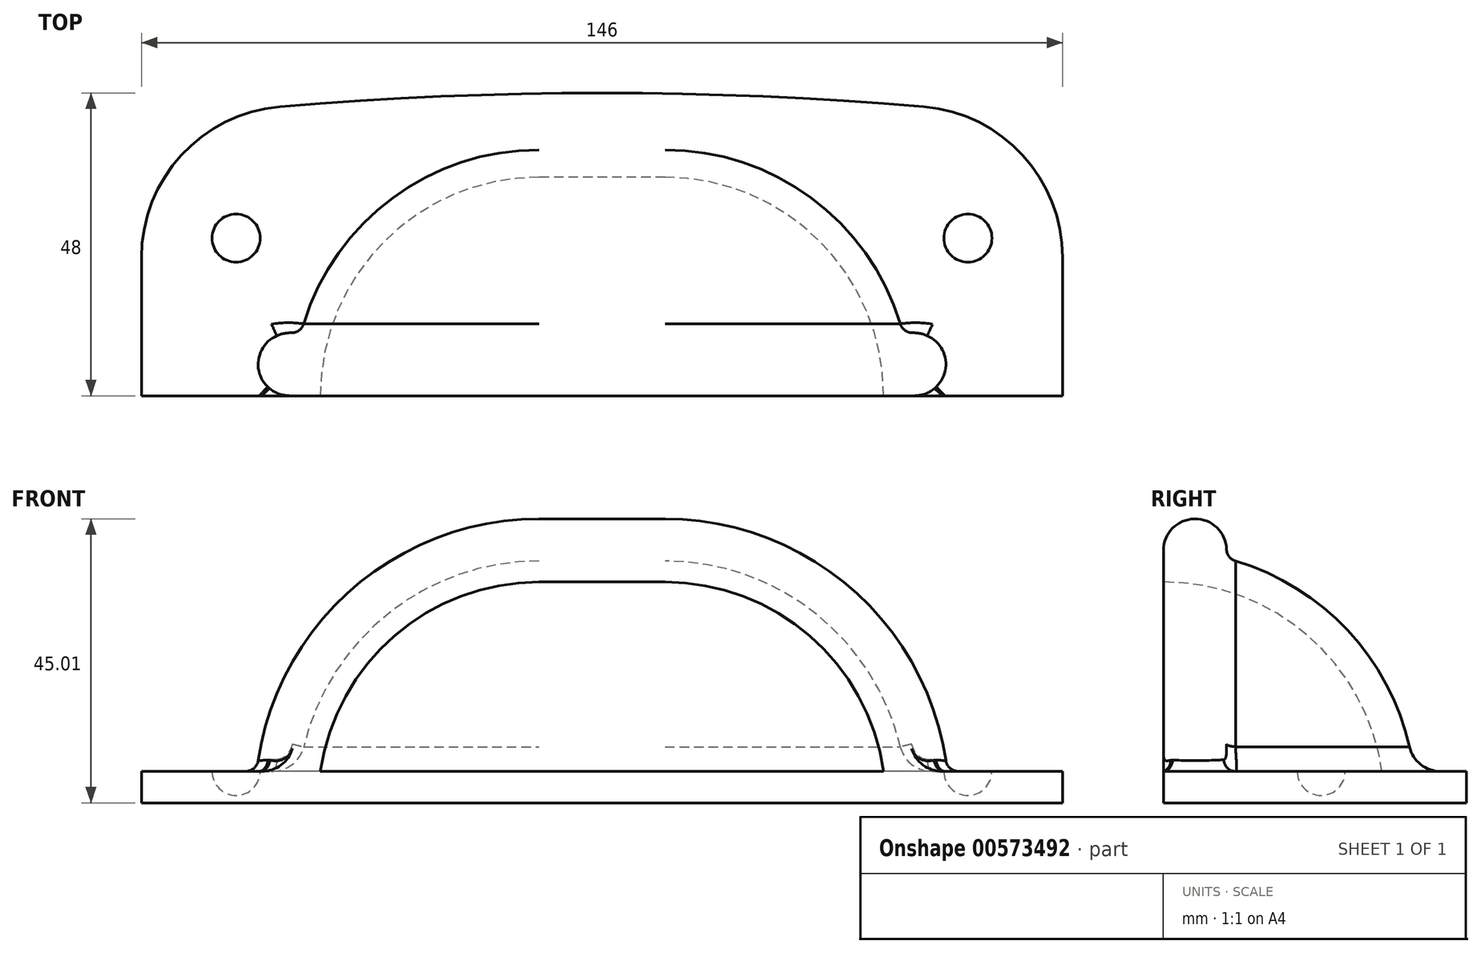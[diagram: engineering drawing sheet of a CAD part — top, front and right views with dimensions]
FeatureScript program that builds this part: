
annotation { "Feature Type Name" : "Feature", "Feature Type Description" : "" }
export const myFeature = defineFeature(function(context is Context, id is Id, definition is map)
    precondition{}
    {
        {
            var Q0;
            Q0=qCreatedBy(makeId("Top.planeOp"),FACE);
            var sketch = newSketch(context, id + "F0", { "sketchPlane" : qUnion([Q0])});
            skLineSegment(sketch, "E0", {"start": v(0, 0) * mm, "end": v(10, 0) * mm, "construction": true});
            skArc(sketch, "E1", {"start": v(10, 35) * mm, "mid": v(34.75, 24.75) * mm, "end": v(45, 0) * mm});
            skLineSegment(sketch, "E2", {"start": v(10, 35) * mm, "end": v(0, 35) * mm});
            skLineSegment(sketch, "E3", {"start": v(45, 0) * mm, "end": v(50, 0) * mm});
            skLineSegment(sketch, "E4.0", {"start": v(10, 40) * mm, "end": v(0, 40) * mm});
            skArc(sketch, "E4.1", {"start": v(10, 40) * mm, "mid": v(38.28, 28.28) * mm, "end": v(50, 0) * mm});
            skLineSegment(sketch, "E5", {"start": v(0, 40) * mm, "end": v(0, 0) * mm, "construction": true});
            skLineSegment(sketch, "E6.MirrorCS", {"start": v(-10, 35) * mm, "end": v(0, 35) * mm});
            skArc(sketch, "E7.MirrorCS", {"start": v(-10, 35) * mm, "mid": v(-34.75, 24.75) * mm, "end": v(-45, 0) * mm});
            skLineSegment(sketch, "E8.MirrorCS", {"start": v(-45, 0) * mm, "end": v(-50, 0) * mm});
            skArc(sketch, "E9.MirrorCS", {"start": v(-10, 40) * mm, "mid": v(-38.28, 28.28) * mm, "end": v(-50, 0) * mm});
            skLineSegment(sketch, "E10.MirrorCS", {"start": v(-10, 40) * mm, "end": v(0, 40) * mm});
            skLineSegment(sketch, "E11.MirrorCS", {"start": v(0, 0) * mm, "end": v(-10, 0) * mm});
            skSolve(sketch);
        }
        {
            var Q0;
            Q0=qSketchRegion(id+"F0",true);
            var Q1;
            Q1=sQuery(id+"F0.wireOp",EDGE,"E0");
            revolve(context, id + "F1", {"entities" : qUnion([Q0]), "axis" : qUnion([Q1]), "revolveType" : RevolveType.ONE_DIRECTION, "angle" : 90 * degree});
        }
        {
            var Q0;
            Q0=qCreatedBy(makeId("Top.planeOp"),FACE);
            var sketch = newSketch(context, id + "F2", { "sketchPlane" : qUnion([Q0])});
            skArc(sketch, "E12", {"start": v(51.04, 45.83) * mm, "mid": v(25.54, 47.46) * mm, "end": v(0, 48) * mm});
            skLineSegment(sketch, "E13", {"start": v(0, 0) * mm, "end": v(0, 48) * mm, "construction": true});
            skLineSegment(sketch, "E14", {"start": v(0, 48) * mm, "end": v(-79.99, 48) * mm, "construction": true});
            skLineSegment(sketch, "E15", {"start": v(0, 0) * mm, "end": v(10, 0) * mm});
            skLineSegment(sketch, "E16", {"start": v(73, 0) * mm, "end": v(73, 21.91) * mm});
            skPoint(sketch, "E17.visualSharp", {"position": v(73, 43.54) * mm});
            skArc(sketch, "E17.filletArc", {"start": v(73, 21.91) * mm, "mid": v(66.68, 38.14) * mm, "end": v(51.04, 45.83) * mm});
            skArc(sketch, "E18.MirrorCS", {"start": v(-51.04, 45.83) * mm, "mid": v(-25.54, 47.46) * mm, "end": v(0, 48) * mm});
            skArc(sketch, "E19.MirrorCS", {"start": v(-73, 21.91) * mm, "mid": v(-66.68, 38.14) * mm, "end": v(-51.04, 45.83) * mm});
            skLineSegment(sketch, "E20.MirrorCS", {"start": v(-73, 0) * mm, "end": v(-73, 21.91) * mm});
            skLineSegment(sketch, "E21.MirrorCS", {"start": v(0, 0) * mm, "end": v(-10, 0) * mm});
            skArc(sketch, "E22.0", {"start": v(-10, 35) * mm, "mid": v(-34.75, 24.75) * mm, "end": v(-45, 0) * mm});
            skLineSegment(sketch, "E22.1", {"start": v(10, 35) * mm, "end": v(-10, 35) * mm});
            skArc(sketch, "E22.2", {"start": v(10, 35) * mm, "mid": v(34.75, 24.75) * mm, "end": v(45, 0) * mm});
            skLineSegment(sketch, "E23.trimOffspring", {"start": v(-45, 0) * mm, "end": v(-73, 0) * mm});
            skLineSegment(sketch, "E24.trimOffspring", {"start": v(45, 0) * mm, "end": v(73, 0) * mm});
            skSolve(sketch);
        }
        {
            var Q0;
            Q0=qSketchRegion(id+"F2",true);
            extrude(context, id + "F3", {"entities" : qUnion([Q0]), "operationType" : NewBodyOperationType.ADD, "depth" : 5 * mm});
        }
        {
            var Q0;
            Q0=qCreatedBy(makeId("Right.planeOp"),FACE);
            var sketch = newSketch(context, id + "F4", { "sketchPlane" : qUnion([Q0])});
            skArc(sketch, "E25.0.0", {"start": v(10, 33.54) * mm, "mid": v(5.05, 34.63) * mm, "end": v(0, 35) * mm});
            skArc(sketch, "E25.0.2", {"start": v(0, 35) * mm, "mid": v(5.05, 34.63) * mm, "end": v(10, 33.54) * mm});
            skLineSegment(sketch, "E26", {"start": v(0, 35) * mm, "end": v(0, 40) * mm});
            skArc(sketch, "E27", {"start": v(0, 40) * mm, "mid": v(5, 45) * mm, "end": v(10, 40) * mm});
            skLineSegment(sketch, "E28", {"start": v(10, 40) * mm, "end": v(10, 33.54) * mm});
            skPoint(sketch, "E29.orphan", {"position": v(35, 0) * mm});
            skSolve(sketch);
        }
        {
            var Q0;
            Q0=makeQuery(id+"F3.boolean.opBoolean","MERGE",FACE,{"derivedFrom":[makeQuery(id+"F1.opRevolve","CAP_FACE",FACE,{"disambiguationData":[OSD([sQuery(id+"F0.wireOp",EDGE,"E1"),sQuery(id+"F0.wireOp",EDGE,"E2"),sQuery(id+"F0.wireOp",EDGE,"E3"),sQuery(id+"F0.wireOp",EDGE,"E4.0"),sQuery(id+"F0.wireOp",EDGE,"E4.1"),sQuery(id+"F0.wireOp",EDGE,"E6.MirrorCS"),sQuery(id+"F0.wireOp",EDGE,"E7.MirrorCS"),sQuery(id+"F0.wireOp",EDGE,"E8.MirrorCS"),sQuery(id+"F0.wireOp",EDGE,"E9.MirrorCS"),sQuery(id+"F0.wireOp",EDGE,"E10.MirrorCS")])],"isStart":false}),makeQuery(id+"F3.opExtrude","SWEPT_FACE",FACE,{"disambiguationData":[OSD([sQuery(id+"F2.wireOp",EDGE,"E23.trimOffspring")])]}),makeQuery(id+"F3.opExtrude","SWEPT_FACE",FACE,{"disambiguationData":[OSD([sQuery(id+"F2.wireOp",EDGE,"E24.trimOffspring")])]})]});
            var sketch = newSketch(context, id + "F5", { "sketchPlane" : qUnion([Q0])});
            skLineSegment(sketch, "E30.0", {"start": v(10, 35) * mm, "end": v(0, 35) * mm});
            skArc(sketch, "E30.1", {"start": v(10, 35) * mm, "mid": v(34.75, 24.75) * mm, "end": v(45, 0) * mm});
            skLineSegment(sketch, "E31", {"start": v(0, 0) * mm, "end": v(0, 35) * mm, "construction": true});
            skPoint(sketch, "E32.orphan", {"position": v(-10, 35) * mm});
            skSolve(sketch);
        }
        {
            var Q0;
            Q0=qSketchRegion(id+"F4",true);
            var Q1;
            Q1=qConstructionFilter(qBodyType(qCreatedBy(id+"F5",EDGE),BodyType.WIRE),ConstructionObject.NO);
            sweep(context, id + "F6", {"profiles" : qUnion([Q0]), "path" : qUnion([Q1])});
        }
        {
            var Q0;
            Q0=makeQuery(id+"F3.boolean.opBoolean","INTERSECT",EDGE,{"derivedFrom":[makeQuery(id+"F1.opRevolve","SWEPT_FACE",FACE,{"disambiguationData":[OSD([sQuery(id+"F0.wireOp",EDGE,"E9.MirrorCS")])]}),makeQuery(id+"F3.opExtrude","CAP_FACE",FACE,{"disambiguationData":[OSD([sQuery(id+"F2.wireOp",EDGE,"E12"),sQuery(id+"F2.wireOp",EDGE,"E15"),sQuery(id+"F2.wireOp",EDGE,"E16"),sQuery(id+"F2.wireOp",EDGE,"E17.filletArc"),sQuery(id+"F2.wireOp",EDGE,"E18.MirrorCS"),sQuery(id+"F2.wireOp",EDGE,"E19.MirrorCS"),sQuery(id+"F2.wireOp",EDGE,"E20.MirrorCS"),sQuery(id+"F2.wireOp",EDGE,"E21.MirrorCS")])],"isStart":false})]});
            fillet(context, id + "F7", {"entities" : qUnion([Q0]), "radius" : 5 * mm, "tangentPropagation" : true, "allowEdgeOverflow" : false});
        }
        {
            var Q0;
            Q0=makeQuery(id+"F6.opSweep","SWEPT_BODY",BODY,{"disambiguationData":[OSD([sQuery(id+"F4.wireOp",EDGE,"E25.0.2"),sQuery(id+"F4.wireOp",EDGE,"E26"),sQuery(id+"F4.wireOp",EDGE,"E27"),sQuery(id+"F4.wireOp",EDGE,"E28"),sQuery(id+"F5.wireOp",EDGE,"E30.1")])]});
            var Q1;
            Q1=qCreatedBy(makeId("Right.planeOp"),FACE);
            mirror(context, id + "F8", {"entities" : qUnion([Q0]), "mirrorPlane" : qUnion([Q1])});
        }
        {
            var Q0;
            Q0=makeQuery(id+"F1.opRevolve","SWEPT_BODY",BODY,{"disambiguationData":[OSD([sQuery(id+"F0.wireOp",EDGE,"E1"),sQuery(id+"F0.wireOp",EDGE,"E2"),sQuery(id+"F0.wireOp",EDGE,"E3"),sQuery(id+"F0.wireOp",EDGE,"E4.0"),sQuery(id+"F0.wireOp",EDGE,"E4.1"),sQuery(id+"F0.wireOp",EDGE,"E6.MirrorCS"),sQuery(id+"F0.wireOp",EDGE,"E7.MirrorCS"),sQuery(id+"F0.wireOp",EDGE,"E8.MirrorCS"),sQuery(id+"F0.wireOp",EDGE,"E9.MirrorCS"),sQuery(id+"F0.wireOp",EDGE,"E10.MirrorCS")])]});
            var Q1;
            Q1=makeQuery(id+"F8.opPattern","COPY",BODY,{"derivedFrom":makeQuery(id+"F6.opSweep","SWEPT_BODY",BODY,{"disambiguationData":[OSD([sQuery(id+"F4.wireOp",EDGE,"E25.0.2"),sQuery(id+"F4.wireOp",EDGE,"E26"),sQuery(id+"F4.wireOp",EDGE,"E27"),sQuery(id+"F4.wireOp",EDGE,"E28"),sQuery(id+"F5.wireOp",EDGE,"E30.1")])]}),"instanceName":"1"});
            var Q2;
            Q2=makeQuery(id+"F6.opSweep","SWEPT_BODY",BODY,{"disambiguationData":[OSD([sQuery(id+"F4.wireOp",EDGE,"E25.0.2"),sQuery(id+"F4.wireOp",EDGE,"E26"),sQuery(id+"F4.wireOp",EDGE,"E27"),sQuery(id+"F4.wireOp",EDGE,"E28"),sQuery(id+"F5.wireOp",EDGE,"E30.1")])]});
            booleanBodies(context, id + "F9", {"operationType" : BooleanOperationType.UNION, "tools" : qUnion([Q0, Q1, Q2])});
        }
        {
            var Q0;
            Q0=makeQuery(id+"F9.opBoolean","INTERSECT",EDGE,{"derivedFrom":[makeQuery(id+"F6.opSweep","SWEPT_FACE",FACE,{"disambiguationData":[OSD([sQuery(id+"F4.wireOp",EDGE,"E28"),sQuery(id+"F5.wireOp",EDGE,"E30.0")])]}),makeQuery(id+"F1.opRevolve","SWEPT_FACE",FACE,{"disambiguationData":[OSD([sQuery(id+"F0.wireOp",EDGE,"E9.MirrorCS")])]})]});
            var Q1;
            {var subQ0=makeQuery(id+"F6.opSweep","SWEPT_EDGE",EDGE,{"disambiguationData":[OSD([sQuery(id+"F4.wireOp",EDGE,"E27"),sQuery(id+"F4.wireOp",EDGE,"E28"),sQuery(id+"F5.wireOp",EDGE,"E30.0")])]});Q1=makeQuery(id+"F9.opBoolean","MERGE",EDGE,{"derivedFrom":[subQ0,makeQuery(id+"F8.opPattern","COPY",EDGE,{"derivedFrom":subQ0,"instanceName":"1"})]});}
            var Q2;
            Q2=makeQuery(id+"F6.opSweep","SWEPT_EDGE",EDGE,{"disambiguationData":[OSD([sQuery(id+"F4.wireOp",EDGE,"E27"),sQuery(id+"F4.wireOp",EDGE,"E28"),sQuery(id+"F5.wireOp",EDGE,"E30.1")])]});
            var Q3;
            Q3=makeQuery(id+"F9.opBoolean","INTERSECT",EDGE,{"derivedFrom":[makeQuery(id+"F7.opFillet","BLEND_FACE",FACE,{"disambiguationData":[OSD([sQuery(id+"F0.wireOp",EDGE,"E9.MirrorCS"),sQuery(id+"F2.wireOp",EDGE,"E12"),sQuery(id+"F2.wireOp",EDGE,"E16"),sQuery(id+"F2.wireOp",EDGE,"E17.filletArc"),sQuery(id+"F2.wireOp",EDGE,"E18.MirrorCS"),sQuery(id+"F2.wireOp",EDGE,"E19.MirrorCS"),sQuery(id+"F2.wireOp",EDGE,"E20.MirrorCS"),sQuery(id+"F2.wireOp",EDGE,"E22.0"),sQuery(id+"F2.wireOp",EDGE,"E22.1"),sQuery(id+"F2.wireOp",EDGE,"E22.2"),sQuery(id+"F2.wireOp",EDGE,"E23.trimOffspring"),sQuery(id+"F2.wireOp",EDGE,"E24.trimOffspring")])]}),makeQuery(id+"F8.opPattern","COPY",FACE,{"derivedFrom":makeQuery(id+"F6.opSweep","SWEPT_FACE",FACE,{"disambiguationData":[OSD([sQuery(id+"F4.wireOp",EDGE,"E27"),sQuery(id+"F5.wireOp",EDGE,"E30.1")])]}),"instanceName":"1"})]});
            var Q4;
            Q4=makeQuery(id+"F8.opPattern","COPY",EDGE,{"derivedFrom":makeQuery(id+"F6.opSweep","SWEPT_EDGE",EDGE,{"disambiguationData":[OSD([sQuery(id+"F4.wireOp",EDGE,"E27"),sQuery(id+"F4.wireOp",EDGE,"E28"),sQuery(id+"F5.wireOp",EDGE,"E30.1")])]}),"instanceName":"1"});
            var Q5;
            Q5=makeQuery(id+"F9.opBoolean","INTERSECT",EDGE,{"derivedFrom":[makeQuery(id+"F6.opSweep","SWEPT_FACE",FACE,{"disambiguationData":[OSD([sQuery(id+"F4.wireOp",EDGE,"E27"),sQuery(id+"F5.wireOp",EDGE,"E30.1")])]}),makeQuery(id+"F7.opFillet","BLEND_FACE",FACE,{"disambiguationData":[OSD([sQuery(id+"F0.wireOp",EDGE,"E4.1"),sQuery(id+"F2.wireOp",EDGE,"E12"),sQuery(id+"F2.wireOp",EDGE,"E16"),sQuery(id+"F2.wireOp",EDGE,"E17.filletArc"),sQuery(id+"F2.wireOp",EDGE,"E18.MirrorCS"),sQuery(id+"F2.wireOp",EDGE,"E19.MirrorCS"),sQuery(id+"F2.wireOp",EDGE,"E20.MirrorCS"),sQuery(id+"F2.wireOp",EDGE,"E22.0"),sQuery(id+"F2.wireOp",EDGE,"E22.1"),sQuery(id+"F2.wireOp",EDGE,"E22.2"),sQuery(id+"F2.wireOp",EDGE,"E23.trimOffspring"),sQuery(id+"F2.wireOp",EDGE,"E24.trimOffspring")])]})]});
            fillet(context, id + "F10", {"entities" : qUnion([Q0, Q1, Q2, Q3, Q4, Q5]), "radius" : 2 * mm, "tangentPropagation" : true, "allowEdgeOverflow" : false});
        }
        {
            var Q0;
            Q0=makeQuery(id+"F3.opExtrude","CAP_FACE",FACE,{"disambiguationData":[OSD([sQuery(id+"F2.wireOp",EDGE,"E12"),sQuery(id+"F2.wireOp",EDGE,"E16"),sQuery(id+"F2.wireOp",EDGE,"E17.filletArc"),sQuery(id+"F2.wireOp",EDGE,"E18.MirrorCS"),sQuery(id+"F2.wireOp",EDGE,"E19.MirrorCS"),sQuery(id+"F2.wireOp",EDGE,"E20.MirrorCS"),sQuery(id+"F2.wireOp",EDGE,"E22.0"),sQuery(id+"F2.wireOp",EDGE,"E22.1"),sQuery(id+"F2.wireOp",EDGE,"E22.2"),sQuery(id+"F2.wireOp",EDGE,"E23.trimOffspring"),sQuery(id+"F2.wireOp",EDGE,"E24.trimOffspring")])],"isStart":false});
            var sketch = newSketch(context, id + "F11", { "sketchPlane" : qUnion([Q0])});
            skArc(sketch, "E33", {"start": v(58, 21.19) * mm, "mid": v(61.81, 25) * mm, "end": v(58, 28.81) * mm});
            skLineSegment(sketch, "E34", {"start": v(58, 25) * mm, "end": v(58, 37.6) * mm, "construction": true});
            skLineSegment(sketch, "E35", {"start": v(58, 25) * mm, "end": v(58, 28.81) * mm});
            skLineSegment(sketch, "E36", {"start": v(58, 25) * mm, "end": v(58, 21.19) * mm});
            skSolve(sketch);
        }
        {
            var Q0;
            Q0=makeQuery(id+"F11.imprint","IMPRINT",FACE,{"disambiguationData":[TD([[makeQuery(id+"F11.imprint","IMPRINT",EDGE,{"derivedFrom":sQuery(id+"F11.wireOp",EDGE,"E33")}),1.0]])]});
            var Q1;
            Q1=sQuery(id+"F11.wireOp",EDGE,"E34");
            revolve(context, id + "F12", {"entities" : qUnion([Q0]), "axis" : qUnion([Q1]), "revolveType" : RevolveType.FULL});
        }
        {
            var Q0;
            Q0=makeQuery(id+"F12.opRevolve","SWEPT_BODY",BODY,{"disambiguationData":[OSD([sQuery(id+"F11.wireOp",EDGE,"E33"),sQuery(id+"F11.wireOp",EDGE,"E35"),sQuery(id+"F11.wireOp",EDGE,"E36")])]});
            var Q1;
            Q1=qCreatedBy(makeId("Right.planeOp"),FACE);
            mirror(context, id + "F13", {"entities" : qUnion([Q0]), "mirrorPlane" : qUnion([Q1])});
        }
        {
            var Q0;
            Q0=makeQuery(id+"F13.opPattern","COPY",BODY,{"derivedFrom":makeQuery(id+"F12.opRevolve","SWEPT_BODY",BODY,{"disambiguationData":[OSD([sQuery(id+"F11.wireOp",EDGE,"E33"),sQuery(id+"F11.wireOp",EDGE,"E35"),sQuery(id+"F11.wireOp",EDGE,"E36")])]}),"instanceName":"1"});
            var Q1;
            Q1=makeQuery(id+"F12.opRevolve","SWEPT_BODY",BODY,{"disambiguationData":[OSD([sQuery(id+"F11.wireOp",EDGE,"E33"),sQuery(id+"F11.wireOp",EDGE,"E35"),sQuery(id+"F11.wireOp",EDGE,"E36")])]});
            var Q2;
            Q2=makeQuery(id+"F1.opRevolve","SWEPT_BODY",BODY,{"disambiguationData":[OSD([sQuery(id+"F0.wireOp",EDGE,"E1"),sQuery(id+"F0.wireOp",EDGE,"E2"),sQuery(id+"F0.wireOp",EDGE,"E3"),sQuery(id+"F0.wireOp",EDGE,"E4.0"),sQuery(id+"F0.wireOp",EDGE,"E4.1"),sQuery(id+"F0.wireOp",EDGE,"E6.MirrorCS"),sQuery(id+"F0.wireOp",EDGE,"E7.MirrorCS"),sQuery(id+"F0.wireOp",EDGE,"E8.MirrorCS"),sQuery(id+"F0.wireOp",EDGE,"E9.MirrorCS"),sQuery(id+"F0.wireOp",EDGE,"E10.MirrorCS")])]});
            booleanBodies(context, id + "F14", {"operationType" : BooleanOperationType.SUBTRACTION, "tools" : qUnion([Q0, Q1]), "targets" : qUnion([Q2])});
        }
        {
            var Q0;
            Q0=qCreatedBy(makeId("Top.planeOp"),FACE);
            var sketch = newSketch(context, id + "F15", { "sketchPlane" : qUnion([Q0])});
            skArc(sketch, "E37.0", {"start": v(-10, 35) * mm, "mid": v(-34.75, 24.75) * mm, "end": v(-45, 0) * mm});
            skLineSegment(sketch, "E37.1", {"start": v(10, 35) * mm, "end": v(-10, 35) * mm});
            skArc(sketch, "E37.2", {"start": v(10, 35) * mm, "mid": v(34.75, 24.75) * mm, "end": v(45, 0) * mm});
            skLineSegment(sketch, "E38", {"start": v(-45, 0) * mm, "end": v(45, 0) * mm});
            skSolve(sketch);
        }
        {
            var Q0;
            Q0=qSketchRegion(id+"F15",true);
            extrude(context, id + "F16", {"entities" : qUnion([Q0]), "operationType" : NewBodyOperationType.ADD, "depth" : 5 * mm});
        }
    });
